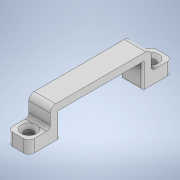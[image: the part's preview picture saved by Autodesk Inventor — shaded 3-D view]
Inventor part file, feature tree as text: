
AUTODESK INVENTOR PART (.ipt)
format: ipt  version: 2021.3 (Build 253353010, 353A)  size: 164,864 bytes
history: native  units: mm
features: fillet x4, sketch x2, projected_geometry x2, extrude x1, hole x1
ambient origin geometry x8: Origin, YZ Plane, XZ Plane, XY Plane, X Axis, Y Axis, Z Axis, Center Point
bodies: Volumenkörper1 (feature_tree)
feature tree (10):
  extrude  "Extrusion1"  Depth=5.0mm
  hole  "Bohrung1"  [1 undecoded]
  fillet  "Rundung1"  Radius=12.0mm
  fillet  "Rundung2"  Radius=13.8mm
  fillet  "Rundung3"  Radius=12.0mm
  fillet  "Rundung4"  Radius=2.0mm
  sketch  "Skizze1"  dims[d0=7.0mm d1=5.0mm]
  sketch  "Skizze2"  dims[d2=4.0mm d3=46.5mm d4=12.0mm d12=13.8mm d13=12.0mm d14=0.0mm d16=5.0mm d17=6.0mm d18=8.6mm d19=2.0mm d20=90.0deg d21=8.0mm d22=20.594885mm d23=2.0mm d24=3.0mm d25=3.0mm d26=1.0mm]
  projected_geometry  "Projizierte Kontur1"
  projected_geometry  "Projizierte Kontur2"
note: 1 required parameter value undecoded (feature->parameter linkage not recoverable at this tier; creation-order binding heuristic only, values carry confidence <= 0.55)
